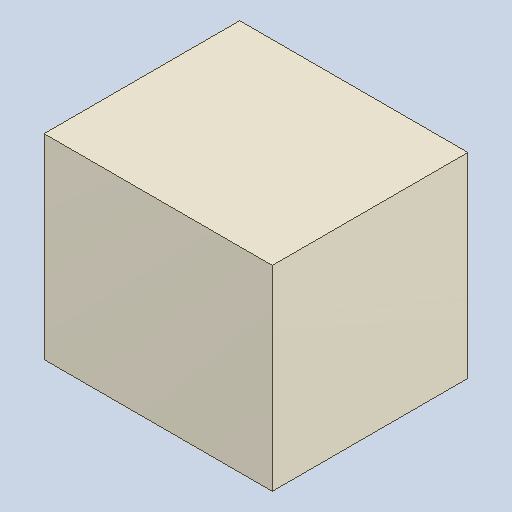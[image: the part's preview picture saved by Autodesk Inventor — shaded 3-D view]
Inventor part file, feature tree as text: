
AUTODESK INVENTOR PART (.ipt)
format: ipt  version: 2023.4 (Build 274418000, 418)  size: 82,432 bytes
history: native  units: mm
features: extrude x1
ambient origin geometry x8: Origin, YZ Plane, XZ Plane, XY Plane, X Axis, Y Axis, Z Axis, Center Point
bodies: Solid1 (feature_tree)
feature tree (1):
  extrude  "Extruded_6"  [1 undecoded]
note: 1 required parameter value undecoded (feature->parameter linkage not recoverable at this tier; creation-order binding heuristic only, values carry confidence <= 0.55)
